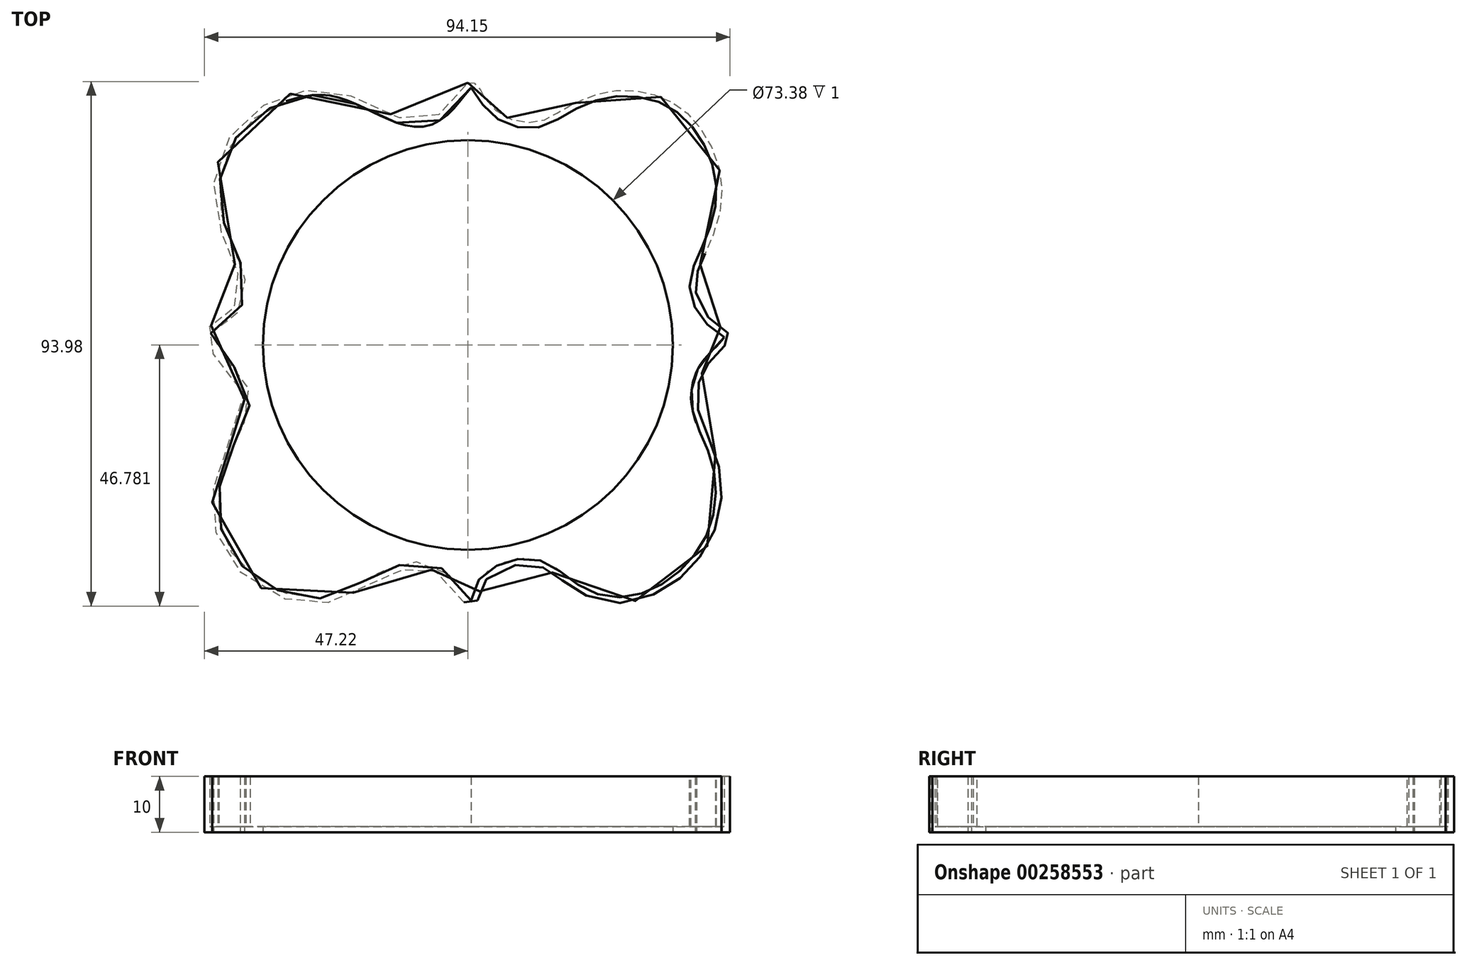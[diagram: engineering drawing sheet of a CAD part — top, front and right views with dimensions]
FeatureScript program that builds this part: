
annotation { "Feature Type Name" : "Feature", "Feature Type Description" : "" }
export const myFeature = defineFeature(function(context is Context, id is Id, definition is map)
    precondition{}
    {
        {
            var Q0;
            Q0=qCreatedBy(makeId("Top.planeOp"),FACE);
            var sketch = newSketch(context, id + "F0", { "sketchPlane" : qUnion([Q0])});
            skFitSpline(sketch, "E0", {"points": [v(0, 43.96) * mm, v(0.72, 44.13) * mm, v(2.02, 43.03) * mm, v(2.81, 41.59) * mm, v(6.23, 38.14) * mm, v(12.34, 36.94) * mm, v(16.12, 38.67) * mm, v(19.57, 40.53) * mm, v(25.35, 42.45) * mm, v(32.86, 41.99) * mm, v(39.2, 38.55) * mm, v(44.13, 31.24) * mm, v(45.25, 21.53) * mm, v(42.16, 12.66) * mm, v(41.17, 10.27) * mm, v(40.75, 6.61) * mm, v(43.56, 1.4) * mm, v(46.8, -1.13) * mm, v(46.66, -2.25) * mm, v(43.7, -5.49) * mm, v(41.74, -8.44) * mm, v(41.03, -13.65) * mm, v(43.56, -20.83) * mm, v(45.33, -27.51) * mm, v(44.27, -35.95) * mm, v(40.48, -42.27) * mm, v(35.2, -46.7) * mm, v(26.35, -49.23) * mm, v(18.34, -46.28) * mm, v(14.76, -43.54) * mm, v(9.7, -42.27) * mm, v(2.74, -45.64) * mm, v(1.48, -49.23) * mm, v(0, -49.65) * mm, v(-4.64, -44.38) * mm, v(-9.28, -42.9) * mm, v(-14.76, -44.38) * mm, v(-21.72, -47.96) * mm, v(-27.83, -49.44) * mm, v(-37.53, -46.28) * mm, v(-44.27, -38.69) * mm, v(-45.75, -30.46) * mm, v(-43, -20.77) * mm, v(-40.27, -11.07) * mm, v(-46.8, -3.06) * mm, v(-46.6, 0) * mm, v(-43.43, 2) * mm, v(-40.9, 6) * mm, v(-41.74, 11.5) * mm, v(-45.12, 20.35) * mm, v(-44.49, 30.68) * mm, v(-38.8, 38.48) * mm, v(-30.78, 42.27) * mm, v(-22.77, 42.27) * mm, v(-12.02, 37.63) * mm, v(-5.27, 38.27) * mm, v(0, 43.96) * mm]});
            skSolve(sketch);
        }
        {
            var Q0;
            Q0=makeQuery(id+"F0.imprint","IMPRINT",FACE,{"disambiguationData":[TD([[makeQuery(id+"F0.imprint","IMPRINT",EDGE,{"derivedFrom":sQuery(id+"F0.wireOp",EDGE,"E0")}),-1.0]])]});
            extrude(context, id + "F1", {"entities" : qUnion([Q0]), "depth" : 10 * mm});
        }
        {
            var Q0;
            Q0=makeQuery(id+"F1.opExtrude","CAP_FACE",FACE,{"disambiguationData":[OSD([sQuery(id+"F0.wireOp",EDGE,"E0")])],"isStart":false});
            shell(context, id + "F2", {"entities" : qUnion([Q0]), "thickness" : 1 * mm});
        }
        {
            var Q0;
            Q0=makeQuery(id+"F0.imprint","IMPRINT",FACE,{"disambiguationData":[TD([[makeQuery(id+"F0.imprint","IMPRINT",EDGE,{"derivedFrom":sQuery(id+"F0.wireOp",EDGE,"E0")}),-1.0]])]});
            var sketch = newSketch(context, id + "F3", { "sketchPlane" : qUnion([Q0])});
            skCircle(sketch, "E1", {"center": v(0, -3) * mm, "radius": 36.7 * mm});
            skSolve(sketch);
        }
        {
            var Q0;
            Q0 = qSketchRegion(id + "F3", true);
            extrude(context, id + "F4", {"entities" : qUnion([Q0]), "operationType" : NewBodyOperationType.REMOVE, "depth" : 25 * mm});
        }
    });
